# Revit family: ESL1107xWS840M9xx
name_source: partatom
category: Leuchten
units: mm (PartAtom-declared; Revit-internal decimal feet)

## family parameters
Basisbauteil = Fläche
Beim Laden mit Abzugskörper schneiden = Nein
Bemaßung runder Anschluss = Durchmesser verwenden
Gemeinsam genutzt = Nein
Lichtquelle = Ja
OmniClass-Nummer = 23.80.70.11
OmniClass-Titel = Luminaries for Internal Lighting
Raumberechnungspunkt = Nein
Teiletyp = Normal

## types (4) — shared parameters
Baugruppenkennzeichen = D5020200
Emissionsform beim Rendern sichtbar = Nein
Farbfilter = 16777215
Farbtemperaturverschiebung bei Dämpfen der Lampe = <Keine Auswahl>
Hersteller = RIDI Leuchten GmbH
Lampe = LED
Neigungswinkel = 90.00°
URL = www.ridi.de
Von Breite des Rechtecks ausssenden = 720 mm  [stored 2.3622 ft]
Von Länge des Rechtecks aussenden = 92 mm  [stored 0.301837 ft]
brand = RIDI
conformity mark = CE
electrical safety class = 1
height = 58 mm  [stored 0.190289 ft]
ingress protection (IP) code = IP20
length = 1107 mm  [stored 3.63189 ft]
nominal frequency = 50-60Hz
nominal voltage = 230
voltage type (AC, DC, UC) = AC
weight = 5,1 kg
width = 330 mm
zero-valued in all types: Vorgabe-Ansicht

## per-type parameters (varying)
| type | Datei für fotometrisches Netz | Modell | Scheinlast | rated input power |
| ESL1107FLWS840M9P0400 | xxxM9Pxxx.IES | 0828162 | 25 VA | 25 |
| ESL1107DAWS840M9P0400 | xxxM9Pxxx.IES | 0838162 | 25 VA | 25 |
| ESL1107FLWS840M9S0350 | xxxM9Sxxx.IES | 0828160 | 25 VA | 25 |
| ESL1107DAWS840M9S0350 | xxxM9Sxxx.IES | 0838160 | 26 VA | 26 |

note: column(s) folded — value = type name in every type: product name

note: [stored X ft] marks values corroborated as IEEE doubles in the binary element streams (Revit-internal decimal feet)
